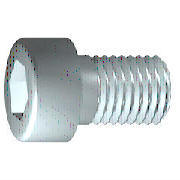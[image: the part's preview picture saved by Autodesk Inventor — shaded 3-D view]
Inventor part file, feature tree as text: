
AUTODESK INVENTOR PART (.ipt)
format: ipt  version: 2020 (Build 240168000, 168)  size: 199,168 bytes
history: native  units: mm (DEFAULTED — no unit token found)
features: sketch x2, extrude x1, plane x1, fillet x1
ambient origin geometry x7: Origin, YZ Plane, XY Plane, X Axis, Y Axis, Z Axis, Center Point
bodies: Solid1 (feature_tree), Body (feature_tree)
feature tree (5):
  extrude  "Slot"  Depth=3.0mm
  plane  "Work Plane1"
  fillet  "Fillet2"  Radius=3.0mm
  sketch  "Sketch1"  dims[d1=6.75mm d2=0.306825mm d3=3.0mm]
  sketch  "Sketch2"  dims[d4=1.3mm d5=60.0deg d6=3.0mm d7=3.0mm d8=2.886751mm d9=5.5mm d10=90.0deg d11=10.0mm d12=0.0mm d13=6.75mm d14=0.0mm d15=0.306725mm d16=0.306725mm d17=0.3mm d19=0.0mm d26=8.0mm d27=45.0deg d28=0.0mm d29=0.0mm d30=0.1mm]
